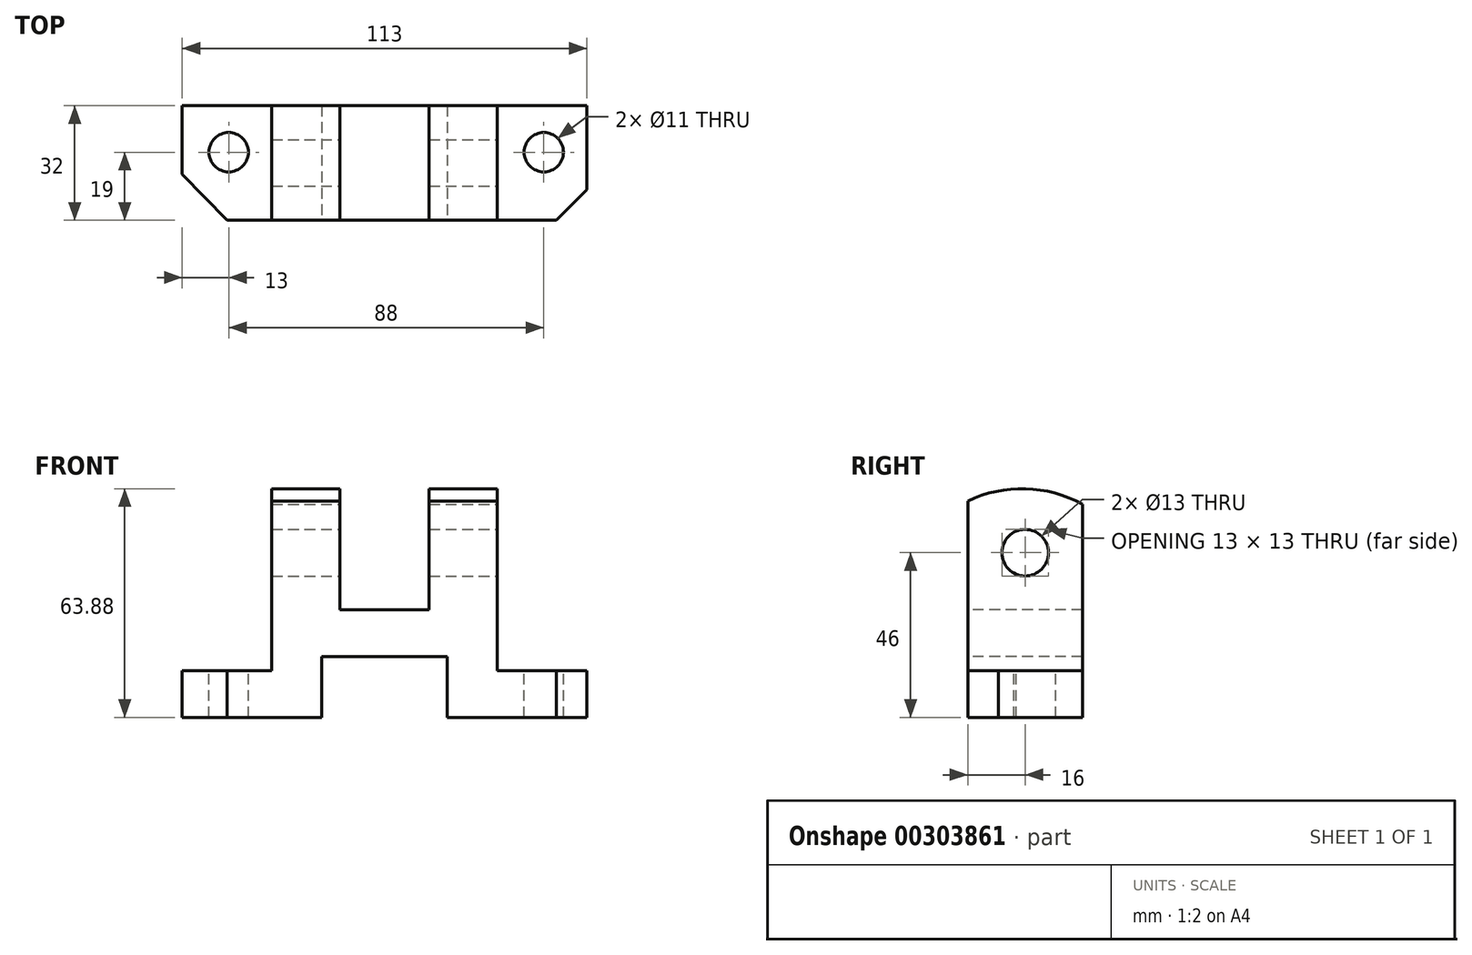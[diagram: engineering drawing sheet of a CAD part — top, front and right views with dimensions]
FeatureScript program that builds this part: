
annotation { "Feature Type Name" : "Feature", "Feature Type Description" : "" }
export const myFeature = defineFeature(function(context is Context, id is Id, definition is map)
    precondition{}
    {
        {
            var Q0;
            Q0=qCreatedBy(makeId("Front.planeOp"),FACE);
            var sketch = newSketch(context, id + "F0", { "sketchPlane" : qUnion([Q0])});
            skLineSegment(sketch, "E0", {"start": v(39, 0) * mm, "end": v(74, 0) * mm});
            skLineSegment(sketch, "E1", {"start": v(74, 0) * mm, "end": v(113, 0) * mm});
            skPoint(sketch, "E1.endSnap0", {"position": v(56.5, 0) * mm});
            skLineSegment(sketch, "E2", {"start": v(113, 0) * mm, "end": v(113, 13) * mm});
            skLineSegment(sketch, "E3", {"start": v(113, 13) * mm, "end": v(88, 13) * mm});
            skLineSegment(sketch, "E4", {"start": v(88, 13) * mm, "end": v(88, 64) * mm});
            skLineSegment(sketch, "E5", {"start": v(88, 64) * mm, "end": v(69, 64) * mm});
            skLineSegment(sketch, "E6", {"start": v(69, 64) * mm, "end": v(69, 30) * mm});
            skLineSegment(sketch, "E7", {"start": v(69, 30) * mm, "end": v(44, 30) * mm});
            skLineSegment(sketch, "E8", {"start": v(44, 30) * mm, "end": v(44, 64) * mm});
            skLineSegment(sketch, "E9", {"start": v(44, 64) * mm, "end": v(25, 64) * mm});
            skLineSegment(sketch, "E10", {"start": v(25, 64) * mm, "end": v(25, 13) * mm});
            skLineSegment(sketch, "E11", {"start": v(0, 0) * mm, "end": v(0, 13) * mm});
            skLineSegment(sketch, "E12", {"start": v(39, 0) * mm, "end": v(0, 0) * mm});
            skLineSegment(sketch, "E13", {"start": v(0, 13) * mm, "end": v(25, 13) * mm});
            skSolve(sketch);
        }
        {
            var Q0;
            Q0 = qSketchRegion(id + "F0", true);
            extrude(context, id + "F1", {"entities" : qUnion([Q0]), "oppositeDirection" : true, "depth" : 32 * mm});
        }
        {
            var Q0;
            Q0=makeQuery(id+"F1.opExtrude","CAP_FACE",FACE,{"disambiguationData":[OSD([sQuery(id+"F0.wireOp",EDGE,"bibvJemU-5A1a-NZ02-wZda-lk2h5ffmCh12"),sQuery(id+"F0.wireOp",EDGE,"E0"),sQuery(id+"F0.wireOp",EDGE,"E1"),sQuery(id+"F0.wireOp",EDGE,"E2"),sQuery(id+"F0.wireOp",EDGE,"E3"),sQuery(id+"F0.wireOp",EDGE,"E4"),sQuery(id+"F0.wireOp",EDGE,"E5"),sQuery(id+"F0.wireOp",EDGE,"E6"),sQuery(id+"F0.wireOp",EDGE,"E7"),sQuery(id+"F0.wireOp",EDGE,"E8"),sQuery(id+"F0.wireOp",EDGE,"E9"),sQuery(id+"F0.wireOp",EDGE,"E10"),sQuery(id+"F0.wireOp",EDGE,"K6n0VZHU-ZGkv-8DcH-riTG-nNLrM5M9xaa2"),sQuery(id+"F0.wireOp",EDGE,"xwuMv6IN-tkBe-M2fu-u9iP-DU3fu6vUG37u")])],"isStart":true});
            var sketch = newSketch(context, id + "F2", { "sketchPlane" : qUnion([Q0])});
            skLineSegment(sketch, "E14", {"start": v(39, 0) * mm, "end": v(74, 0) * mm});
            skLineSegment(sketch, "E15", {"start": v(74, 0) * mm, "end": v(74, 17) * mm});
            skLineSegment(sketch, "E16", {"start": v(74, 17) * mm, "end": v(39, 17) * mm});
            skLineSegment(sketch, "E17", {"start": v(39, 17) * mm, "end": v(39, 0) * mm});
            skSolve(sketch);
        }
        {
            var Q0;
            Q0=makeQuery(id+"F1.opExtrude","SWEPT_FACE",FACE,{"disambiguationData":[OSD([sQuery(id+"F0.wireOp",EDGE,"E3")])]});
            var sketch = newSketch(context, id + "F3", { "sketchPlane" : qUnion([Q0])});
            skPoint(sketch, "E18.endSnap0", {"position": v(88, 16) * mm});
            skLineSegment(sketch, "E19", {"start": v(88, 32) * mm, "end": v(88, 19) * mm});
            skLineSegment(sketch, "E20", {"start": v(88, 19) * mm, "end": v(101, 19) * mm});
            skCircle(sketch, "E21", {"center": v(101, 19) * mm, "radius": 5.5 * mm});
            skLineSegment(sketch, "E22", {"start": v(0, 0) * mm, "end": v(0, 19) * mm});
            skLineSegment(sketch, "E23", {"start": v(0, 19) * mm, "end": v(13, 19) * mm});
            skCircle(sketch, "E24", {"center": v(13, 19) * mm, "radius": 5.5 * mm});
            skSolve(sketch);
        }
        {
            var Q0;
            Q0 = qSketchRegion(id + "F2", true);
            extrude(context, id + "F4", {"entities" : qUnion([Q0]), "operationType" : NewBodyOperationType.REMOVE, "oppositeDirection" : true, "depth" : 32 * mm});
        }
        {
            var Q0;
            Q0=makeQuery(id+"F3.imprint","IMPRINT",FACE,{"disambiguationData":[TD([[makeQuery(id+"F3.imprint","IMPRINT",EDGE,{"derivedFrom":sQuery(id+"F3.wireOp",EDGE,"E21")}),1.0]])]});
            var Q1;
            Q1=makeQuery(id+"F3.imprint","IMPRINT",FACE,{"disambiguationData":[TD([[makeQuery(id+"F3.imprint","IMPRINT",EDGE,{"derivedFrom":sQuery(id+"F3.wireOp",EDGE,"E24")}),1.0]])]});
            var Q2;
            Q2=sQuery(id+"F3.wireOp",EDGE,"E21");
            var Q3;
            Q3=sQuery(id+"F3.wireOp",EDGE,"E24");
            extrude(context, id + "F5", {"entities" : qUnion([Q0, Q1]), "operationType" : NewBodyOperationType.REMOVE, "surfaceEntities" : qUnion([Q2, Q3]), "oppositeDirection" : true, "depth" : 25 * mm});
        }
        {
            var Q0;
            Q0=makeQuery(id+"F1.opExtrude","SWEPT_FACE",FACE,{"disambiguationData":[OSD([sQuery(id+"F0.wireOp",EDGE,"E4")])]});
            var sketch = newSketch(context, id + "F6", { "sketchPlane" : qUnion([Q0])});
            skLineSegment(sketch, "E25", {"start": v(0, 0) * mm, "end": v(16, 0) * mm, "construction": true});
            skLineSegment(sketch, "E26", {"start": v(16, 0) * mm, "end": v(16, 46) * mm, "construction": true});
            skCircle(sketch, "E27", {"center": v(16, 46) * mm, "radius": 6.5 * mm});
            skSolve(sketch);
        }
        {
            var Q0;
            Q0=makeQuery(id+"F6.imprint","IMPRINT",FACE,{"disambiguationData":[TD([[makeQuery(id+"F6.imprint","IMPRINT",EDGE,{"derivedFrom":sQuery(id+"F6.wireOp",EDGE,"E27")}),1.0]])]});
            var Q1;
            Q1=sQuery(id+"F6.wireOp",EDGE,"E27");
            extrude(context, id + "F7", {"entities" : qUnion([Q0]), "operationType" : NewBodyOperationType.REMOVE, "surfaceEntities" : qUnion([Q1]), "oppositeDirection" : true, "depth" : 80 * mm});
        }
        {
            var Q0;
            Q0=makeQuery(id+"F1.opExtrude","SWEPT_FACE",FACE,{"disambiguationData":[OSD([sQuery(id+"F0.wireOp",EDGE,"E4")])]});
            var sketch = newSketch(context, id + "F8", { "sketchPlane" : qUnion([Q0])});
            skArc(sketch, "E28", {"start": v(32, 59.53) * mm, "mid": v(16.11, 63.87) * mm, "end": v(0, 60.45) * mm});
            skLineSegment(sketch, "E29", {"start": v(0, 60.45) * mm, "end": v(0, 64) * mm});
            skLineSegment(sketch, "E30", {"start": v(0, 64) * mm, "end": v(32, 64) * mm});
            skLineSegment(sketch, "E31", {"start": v(32, 64) * mm, "end": v(32, 59.53) * mm});
            skSolve(sketch);
        }
        {
            var Q0;
            Q0=makeQuery(id+"F8.imprint","IMPRINT",FACE,{"disambiguationData":[TD([[makeQuery(id+"F8.imprint","IMPRINT",EDGE,{"derivedFrom":sQuery(id+"F8.wireOp",EDGE,"E28")}),-1.0]])]});
            extrude(context, id + "F9", {"entities" : qUnion([Q0]), "operationType" : NewBodyOperationType.REMOVE, "oppositeDirection" : true, "depth" : 80 * mm});
        }
        {
            var Q0;
            {var subQ3=sQuery(id+"F3.wireOp",EDGE,"E19");Q0=makeQuery(id+"F3.imprint","IMPRINT",FACE,{"disambiguationData":[TD([[makeQuery(id+"F3.imprint","IMPRINT",EDGE,{"derivedFrom":subQ3}),1.0]])]});}
            var sketch = newSketch(context, id + "F10", { "sketchPlane" : qUnion([Q0])});
            skLineSegment(sketch, "E32", {"start": v(114.47, 0) * mm, "end": v(104.47, 0) * mm});
            skLineSegment(sketch, "E33", {"start": v(104.47, 0) * mm, "end": v(115.57, 11.1) * mm});
            skLineSegment(sketch, "E34", {"start": v(115.57, 11.1) * mm, "end": v(114.47, 0) * mm});
            skSolve(sketch);
        }
        {
            var Q0;
            {var subQ0=sQuery(id+"F10.wireOp",EDGE,"E32");var subQ1=sQuery(id+"F0.wireOp",EDGE,"E3");var subQ2=makeQuery(id+"F3.imprint","IMPRINT",EDGE,{"derivedFrom":makeQuery(id+"F1.opExtrude","SWEPT_EDGE",EDGE,{"disambiguationData":[OSD([sQuery(id+"F0.wireOp",EDGE,"E2"),subQ1])]})});var subQ3=makeQuery(id+"F10.imprint","INTERSECT",VERTEX,{"derivedFrom":[subQ2,subQ0]});Q0=makeQuery(id+"F10.imprint","IMPRINT",FACE,{"disambiguationData":[TD([[makeQuery(id+"F10.imprint","IMPRINT",EDGE,{"disambiguationData":[TD([[subQ3,-1.0]])],"derivedFrom":subQ0}),-1.0]])]});}
            extrude(context, id + "F11", {"entities" : qUnion([Q0]), "operationType" : NewBodyOperationType.REMOVE, "oppositeDirection" : true, "depth" : 25 * mm});
        }
        {
            var Q0;
            Q0=makeQuery(id+"F1.opExtrude","SWEPT_FACE",FACE,{"disambiguationData":[OSD([sQuery(id+"F0.wireOp",EDGE,"E13")])]});
            var sketch = newSketch(context, id + "F12", { "sketchPlane" : qUnion([Q0])});
            skLineSegment(sketch, "E35", {"start": v(0, 0) * mm, "end": v(12.5, 0) * mm});
            skLineSegment(sketch, "E36", {"start": v(12.5, 0) * mm, "end": v(0, 12.87) * mm});
            skLineSegment(sketch, "E37", {"start": v(0, 12.87) * mm, "end": v(0, 0) * mm});
            skSolve(sketch);
        }
        {
            var Q0;
            Q0=makeQuery(id+"F12.imprint","IMPRINT",FACE,{"disambiguationData":[TD([[makeQuery(id+"F12.imprint","IMPRINT",EDGE,{"derivedFrom":sQuery(id+"F12.wireOp",EDGE,"E35")}),1.0]])]});
            extrude(context, id + "F13", {"entities" : qUnion([Q0]), "operationType" : NewBodyOperationType.REMOVE, "oppositeDirection" : true, "depth" : 25 * mm});
        }
    });
